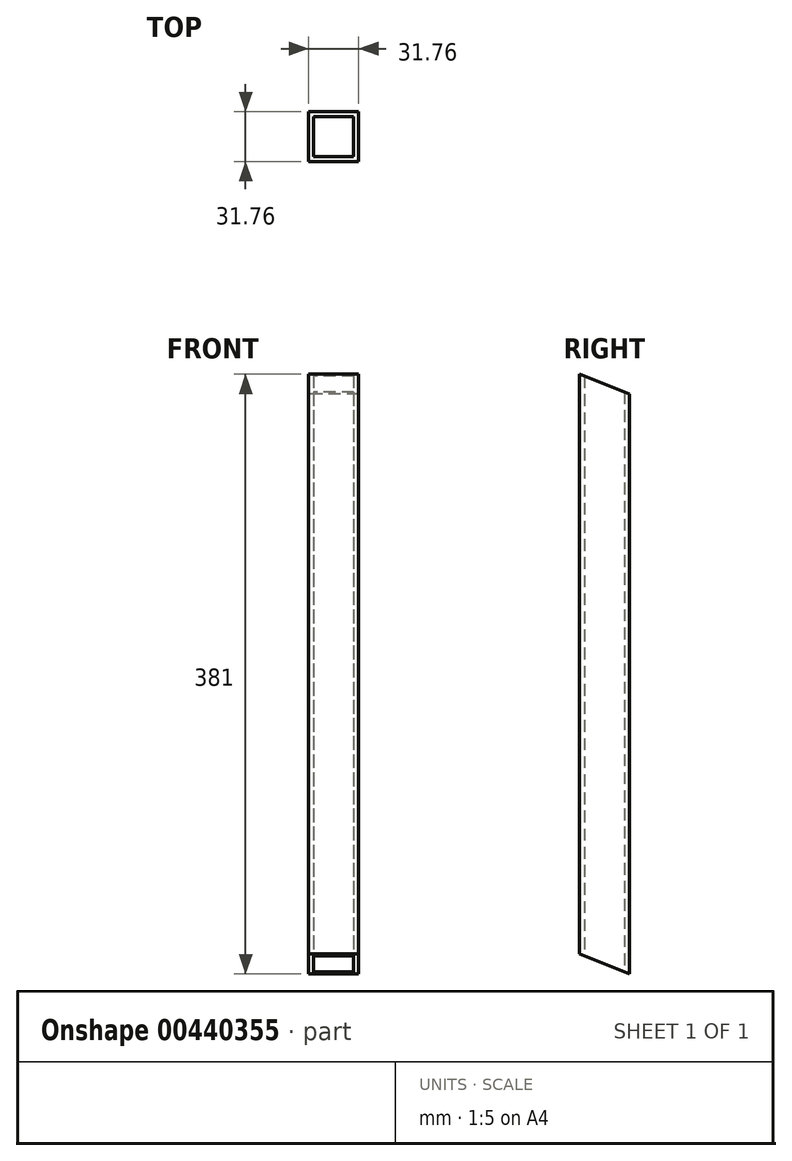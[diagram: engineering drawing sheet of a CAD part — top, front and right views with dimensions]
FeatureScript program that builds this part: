
annotation { "Feature Type Name" : "Feature", "Feature Type Description" : "" }
export const myFeature = defineFeature(function(context is Context, id is Id, definition is map)
    precondition{}
    {
        {
            var Q0;
            Q0=qCreatedBy(makeId("Top.planeOp"),FACE);
            var sketch = newSketch(context, id + "F0", { "sketchPlane" : qUnion([Q0])});
            skLineSegment(sketch, "E0.bottom", {"start": v(-15.87, 15.88) * mm, "end": v(15.88, 15.88) * mm});
            skLineSegment(sketch, "E0.top", {"start": v(-15.88, -15.88) * mm, "end": v(15.87, -15.88) * mm});
            skLineSegment(sketch, "E0.left", {"start": v(-15.87, 15.88) * mm, "end": v(-15.88, -15.88) * mm});
            skLineSegment(sketch, "E0.right", {"start": v(15.88, 15.88) * mm, "end": v(15.87, -15.88) * mm});
            skPoint(sketch, "E0.middle", {"position": v(0, 0) * mm});
            skLineSegment(sketch, "E1.bottom", {"start": v(-12.7, 12.7) * mm, "end": v(12.7, 12.7) * mm});
            skLineSegment(sketch, "E1.top", {"start": v(-12.7, -12.7) * mm, "end": v(12.7, -12.7) * mm});
            skLineSegment(sketch, "E1.left", {"start": v(-12.7, 12.7) * mm, "end": v(-12.7, -12.7) * mm});
            skLineSegment(sketch, "E1.right", {"start": v(12.7, 12.7) * mm, "end": v(12.7, -12.7) * mm});
            skSolve(sketch);
        }
        {
            var Q0;
            Q0=makeQuery(id+"F0.imprint","IMPRINT",FACE,{"disambiguationData":[TD([[makeQuery(id+"F0.imprint","IMPRINT",EDGE,{"derivedFrom":sQuery(id+"F0.wireOp",EDGE,"E0.bottom")}),-1.0]])]});
            extrude(context, id + "F1", {"entities" : qUnion([Q0]), "endBound" : BoundingType.SYMMETRIC, "depth" : 381 * mm});
        }
        {
            var Q0;
            Q0=makeQuery(id+"F1.opExtrude","SWEPT_FACE",FACE,{"disambiguationData":[OSD([sQuery(id+"F0.wireOp",EDGE,"E0.left")])]});
            var sketch = newSketch(context, id + "F2", { "sketchPlane" : qUnion([Q0])});
            skLineSegment(sketch, "E2", {"start": v(-15.87, 190.5) * mm, "end": v(-15.87, 177.8) * mm});
            skLineSegment(sketch, "E3", {"start": v(-15.87, 177.8) * mm, "end": v(15.88, 190.5) * mm});
            skSolve(sketch);
        }
        {
            var Q0;
            Q0=makeQuery(id+"F2.imprint","IMPRINT",FACE,{"disambiguationData":[TD([[makeQuery(id+"F2.imprint","IMPRINT",EDGE,{"derivedFrom":sQuery(id+"F2.wireOp",EDGE,"E2")}),1.0]])]});
            extrude(context, id + "F3", {"entities" : qUnion([Q0]), "operationType" : NewBodyOperationType.REMOVE, "oppositeDirection" : true, "depth" : 31.75 * mm});
        }
        {
            var Q0;
            Q0=makeQuery(id+"F1.opExtrude","SWEPT_FACE",FACE,{"disambiguationData":[OSD([sQuery(id+"F0.wireOp",EDGE,"E0.left")])]});
            var sketch = newSketch(context, id + "F4", { "sketchPlane" : qUnion([Q0])});
            skLineSegment(sketch, "E4", {"start": v(15.88, -190.5) * mm, "end": v(15.88, -177.8) * mm});
            skLineSegment(sketch, "E5", {"start": v(15.88, -177.8) * mm, "end": v(-15.87, -190.5) * mm});
            skSolve(sketch);
        }
        {
            var Q0;
            Q0=makeQuery(id+"F4.imprint","IMPRINT",FACE,{"disambiguationData":[TD([[makeQuery(id+"F4.imprint","IMPRINT",EDGE,{"derivedFrom":sQuery(id+"F4.wireOp",EDGE,"E4")}),-1.0]])]});
            extrude(context, id + "F5", {"entities" : qUnion([Q0]), "operationType" : NewBodyOperationType.REMOVE, "oppositeDirection" : true, "depth" : 31.75 * mm});
        }
    });
